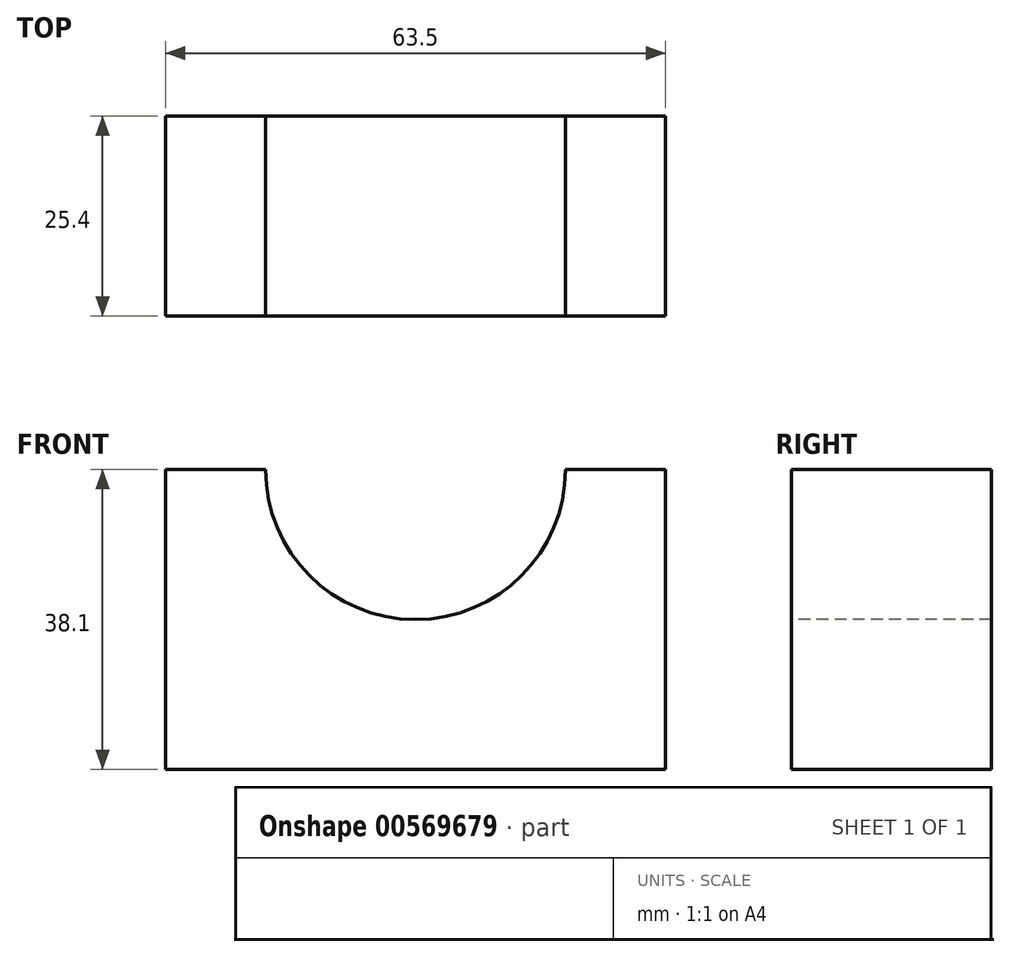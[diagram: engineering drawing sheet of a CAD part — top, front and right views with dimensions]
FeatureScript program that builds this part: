
annotation { "Feature Type Name" : "Feature", "Feature Type Description" : "" }
export const myFeature = defineFeature(function(context is Context, id is Id, definition is map)
    precondition{}
    {
        {
            var Q0;
            Q0=qCreatedBy(makeId("Top.planeOp"),FACE);
            var sketch = newSketch(context, id + "F0", { "sketchPlane" : qUnion([Q0])});
            skLineSegment(sketch, "E0.bottom", {"start": v(-46.48, -34.62) * mm, "end": v(17.02, -34.62) * mm});
            skLineSegment(sketch, "E0.top", {"start": v(-46.48, -9.22) * mm, "end": v(17.02, -9.22) * mm});
            skLineSegment(sketch, "E0.left", {"start": v(-46.48, -34.62) * mm, "end": v(-46.48, -9.22) * mm});
            skLineSegment(sketch, "E0.right", {"start": v(17.02, -34.62) * mm, "end": v(17.02, -9.22) * mm});
            skSolve(sketch);
        }
        {
            var Q0;
            Q0 = qSketchRegion(id + "F0", true);
            extrude(context, id + "F1", {"entities" : qUnion([Q0]), "depth" : 38.1 * mm, "offsetDistance" : 25.4 * mm});
        }
        {
            var Q0;
            Q0=makeQuery(id+"F1.opExtrude","SWEPT_FACE",FACE,{"disambiguationData":[OSD([sQuery(id+"F0.wireOp",EDGE,"E0.bottom")])]});
            var sketch = newSketch(context, id + "F2", { "sketchPlane" : qUnion([Q0])});
            skCircle(sketch, "E1", {"center": v(-14.73, 38.1) * mm, "radius": 19.05 * mm});
            skSolve(sketch);
        }
        {
            var Q0;
            {var subQ0=sQuery(id+"F2.wireOp",EDGE,"E1");var subQ1=makeQuery(id+"F1.opExtrude","CAP_EDGE",EDGE,{"disambiguationData":[OSD([sQuery(id+"F0.wireOp",EDGE,"E0.bottom")])],"isStart":false});var subQ2=makeQuery(id+"F2.imprint","INTERSECT",VERTEX,{"disambiguationData":[OD(0.0)],"derivedFrom":[subQ1,subQ0]});Q0=makeQuery(id+"F2.imprint","IMPRINT",FACE,{"disambiguationData":[TD([[makeQuery(id+"F2.imprint","IMPRINT",EDGE,{"disambiguationData":[TD([[subQ2,-1.0]])],"derivedFrom":subQ0}),1.0]])]});}
            var sketch = newSketch(context, id + "F3", { "sketchPlane" : qUnion([Q0])});
            skSolve(sketch);
        }
        {
            var Q0;
            Q0 = qSketchRegion(id + "F3", true);
            var Q1;
            {var subQ0=sQuery(id+"F2.wireOp",EDGE,"E1");var subQ1=makeQuery(id+"F1.opExtrude","CAP_EDGE",EDGE,{"disambiguationData":[OSD([sQuery(id+"F0.wireOp",EDGE,"E0.bottom")])],"isStart":false});var subQ2=makeQuery(id+"F2.imprint","INTERSECT",VERTEX,{"disambiguationData":[OD(0.0)],"derivedFrom":[subQ1,subQ0]});Q1=makeQuery(id+"F2.imprint","IMPRINT",FACE,{"disambiguationData":[TD([[makeQuery(id+"F2.imprint","IMPRINT",EDGE,{"disambiguationData":[TD([[subQ2,-1.0]])],"derivedFrom":subQ0}),1.0]])]});}
            extrude(context, id + "F4", {"entities" : qUnion([Q0, Q1]), "operationType" : NewBodyOperationType.REMOVE, "oppositeDirection" : true, "depth" : 25.4 * mm, "offsetDistance" : 25.4 * mm});
        }
    });
